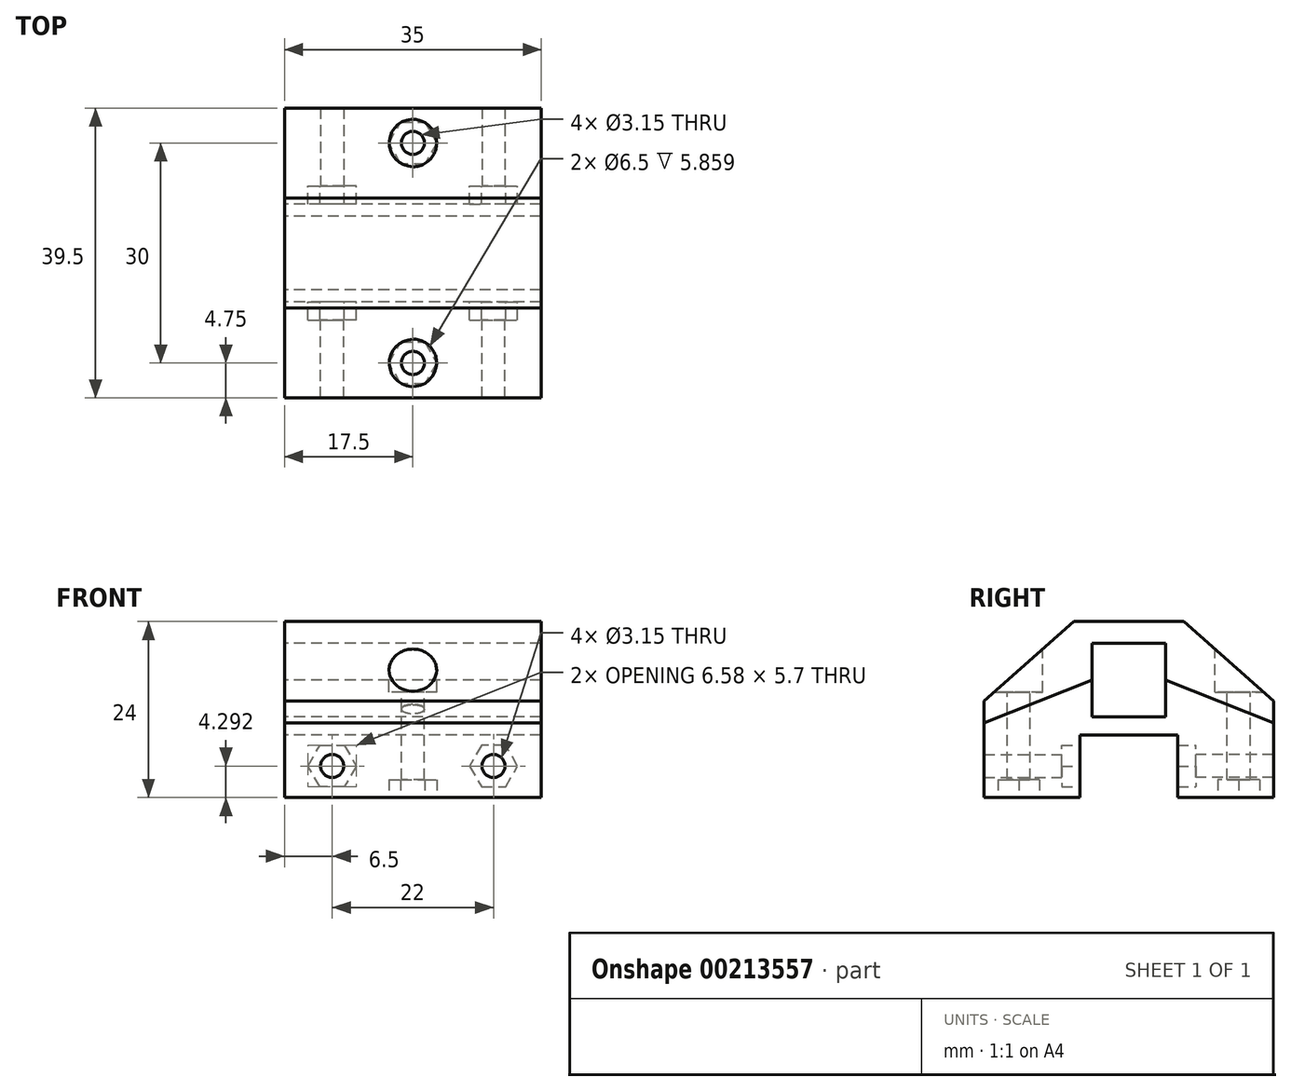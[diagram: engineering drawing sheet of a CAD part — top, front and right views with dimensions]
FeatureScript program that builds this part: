
annotation { "Feature Type Name" : "Feature", "Feature Type Description" : "" }
export const myFeature = defineFeature(function(context is Context, id is Id, definition is map)
    precondition{}
    {
        {
            var Q0;
            Q0=qCreatedBy(makeId("Right.planeOp"),FACE);
            var sketch = newSketch(context, id + "F0", { "sketchPlane" : qUnion([Q0])});
            skLineSegment(sketch, "E0", {"start": v(0, 5) * mm, "end": v(-5, 5) * mm});
            skLineSegment(sketch, "E1", {"start": v(-5, 5) * mm, "end": v(-5, 0) * mm});
            skLineSegment(sketch, "E2", {"start": v(-5, 0) * mm, "end": v(-19.75, -5.85) * mm});
            skLineSegment(sketch, "E3", {"start": v(-19.75, -5.85) * mm, "end": v(-19.75, -2.85) * mm});
            skLineSegment(sketch, "E4", {"start": v(-19.75, -2.85) * mm, "end": v(-7.5, 8) * mm});
            skLineSegment(sketch, "E5", {"start": v(-7.5, 8) * mm, "end": v(0, 8) * mm});
            skLineSegment(sketch, "E6.MirrorCS", {"start": v(5, 0) * mm, "end": v(19.75, -5.85) * mm});
            skLineSegment(sketch, "E7.MirrorCS", {"start": v(19.75, -5.85) * mm, "end": v(19.75, -2.85) * mm});
            skLineSegment(sketch, "E8.MirrorCS", {"start": v(5, 5) * mm, "end": v(5, 0) * mm});
            skLineSegment(sketch, "E9.MirrorCS", {"start": v(0, 5) * mm, "end": v(5, 5) * mm});
            skLineSegment(sketch, "E10.MirrorCS", {"start": v(7.5, 8) * mm, "end": v(0, 8) * mm});
            skLineSegment(sketch, "E11.MirrorCS", {"start": v(19.75, -2.85) * mm, "end": v(7.5, 8) * mm});
            skSolve(sketch);
        }
        {
            var Q0;
            Q0=qCreatedBy(makeId("Right.planeOp"),FACE);
            var sketch = newSketch(context, id + "F1", { "sketchPlane" : qUnion([Q0])});
            skLineSegment(sketch, "E12", {"start": v(-5, 0) * mm, "end": v(-5, -5) * mm});
            skLineSegment(sketch, "E13", {"start": v(-5, -5) * mm, "end": v(0, -5) * mm});
            skLineSegment(sketch, "E14", {"start": v(0, -5) * mm, "end": v(0, -7.5) * mm});
            skLineSegment(sketch, "E15", {"start": v(0, -7.5) * mm, "end": v(-6.66, -7.5) * mm});
            skLineSegment(sketch, "E16", {"start": v(-6.66, -7.5) * mm, "end": v(-6.66, -16) * mm});
            skLineSegment(sketch, "E17", {"start": v(-6.66, -16) * mm, "end": v(-19.75, -16) * mm});
            skLineSegment(sketch, "E18", {"start": v(-19.75, -16) * mm, "end": v(-19.75, -5.8) * mm});
            skLineSegment(sketch, "E19", {"start": v(-19.75, -5.8) * mm, "end": v(-5, 0) * mm});
            skLineSegment(sketch, "E20.MirrorCS", {"start": v(6.66, -7.5) * mm, "end": v(6.66, -16) * mm});
            skLineSegment(sketch, "E21.MirrorCS", {"start": v(6.66, -16) * mm, "end": v(19.75, -16) * mm});
            skLineSegment(sketch, "E22.MirrorCS", {"start": v(19.75, -5.8) * mm, "end": v(5, 0) * mm});
            skLineSegment(sketch, "E23.MirrorCS", {"start": v(0, -7.5) * mm, "end": v(6.66, -7.5) * mm});
            skLineSegment(sketch, "E24.MirrorCS", {"start": v(19.75, -16) * mm, "end": v(19.75, -5.8) * mm});
            skLineSegment(sketch, "E25.MirrorCS", {"start": v(5, 0) * mm, "end": v(5, -5) * mm});
            skLineSegment(sketch, "E26.MirrorCS", {"start": v(5, -5) * mm, "end": v(0, -5) * mm});
            skSolve(sketch);
        }
        {
            var Q0;
            Q0 = qSketchRegion(id + "F1", true);
            extrude(context, id + "F2", {"entities" : qUnion([Q0]), "endBound" : BoundingType.SYMMETRIC, "depth" : 35 * mm});
        }
        {
            var Q0;
            Q0=makeQuery(id+"F0.imprint","IMPRINT",FACE,{"disambiguationData":[TD([[makeQuery(id+"F0.imprint","IMPRINT",EDGE,{"derivedFrom":sQuery(id+"F0.wireOp",EDGE,"E0")}),-1.0]])]});
            extrude(context, id + "F3", {"entities" : qUnion([Q0]), "endBound" : BoundingType.SYMMETRIC, "depth" : 35 * mm});
        }
        {
            var Q0;
            Q0=qCreatedBy(makeId("Front.planeOp"),FACE);
            var sketch = newSketch(context, id + "F4", { "sketchPlane" : qUnion([Q0])});
            skLineSegment(sketch, "E27", {"start": v(0, -11.7) * mm, "end": v(-11, -11.7) * mm});
            skLineSegment(sketch, "E28", {"start": v(0, -11.7) * mm, "end": v(11, -11.7) * mm});
            skCircle(sketch, "E29.cCircle", {"center": v(-11, -11.7) * mm, "radius": 2.85 * mm, "construction": true});
            skLineSegment(sketch, "E29.0", {"start": v(-9.35, -14.56) * mm, "end": v(-12.65, -14.56) * mm});
            skLineSegment(sketch, "E29.1", {"start": v(-12.65, -14.56) * mm, "end": v(-14.3, -11.7) * mm});
            skLineSegment(sketch, "E29.2", {"start": v(-14.3, -11.7) * mm, "end": v(-12.65, -8.86) * mm});
            skLineSegment(sketch, "E29.3", {"start": v(-12.65, -8.86) * mm, "end": v(-9.35, -8.86) * mm});
            skLineSegment(sketch, "E29.4", {"start": v(-9.35, -8.86) * mm, "end": v(-7.7, -11.7) * mm});
            skLineSegment(sketch, "E29.5", {"start": v(-7.7, -11.7) * mm, "end": v(-9.35, -14.56) * mm});
            skPoint(sketch, "E29.0.midPoint", {"position": v(-11, -14.56) * mm});
            skLineSegment(sketch, "E30.MirrorCS", {"start": v(9.35, -14.56) * mm, "end": v(12.65, -14.56) * mm});
            skLineSegment(sketch, "E31.MirrorCS", {"start": v(12.65, -14.56) * mm, "end": v(14.3, -11.7) * mm});
            skPoint(sketch, "E32.MirrorP", {"position": v(11, -14.56) * mm});
            skLineSegment(sketch, "E33.MirrorCS", {"start": v(14.3, -11.7) * mm, "end": v(12.65, -8.86) * mm});
            skLineSegment(sketch, "E34.MirrorCS", {"start": v(7.7, -11.7) * mm, "end": v(9.35, -14.56) * mm});
            skLineSegment(sketch, "E35.MirrorCS", {"start": v(12.65, -8.86) * mm, "end": v(9.35, -8.86) * mm});
            skLineSegment(sketch, "E36.MirrorCS", {"start": v(9.35, -8.86) * mm, "end": v(7.7, -11.7) * mm});
            skCircle(sketch, "E37.MirrorC", {"center": v(11, -11.7) * mm, "radius": 2.85 * mm, "construction": true});
            skSolve(sketch);
        }
        {
            var Q0;
            Q0=sQuery(id+"F4.wireOp",VERTEX,"E27.end");
            var Q1;
            Q1=sQuery(id+"F4.wireOp",VERTEX,"E28.end");
            var Q2;
            Q2=makeQuery(id+"F2.opExtrude","SWEPT_BODY",BODY,{"disambiguationData":[OSD([sQuery(id+"F1.wireOp",EDGE,"E12"),sQuery(id+"F1.wireOp",EDGE,"E13"),sQuery(id+"F1.wireOp",EDGE,"E15"),sQuery(id+"F1.wireOp",EDGE,"E16"),sQuery(id+"F1.wireOp",EDGE,"E17"),sQuery(id+"F1.wireOp",EDGE,"E18"),sQuery(id+"F1.wireOp",EDGE,"E19"),sQuery(id+"F1.wireOp",EDGE,"E20.MirrorCS"),sQuery(id+"F1.wireOp",EDGE,"E21.MirrorCS"),sQuery(id+"F1.wireOp",EDGE,"E22.MirrorCS"),sQuery(id+"F1.wireOp",EDGE,"E23.MirrorCS"),sQuery(id+"F1.wireOp",EDGE,"E24.MirrorCS"),sQuery(id+"F1.wireOp",EDGE,"E25.MirrorCS"),sQuery(id+"F1.wireOp",EDGE,"E26.MirrorCS")])]});
            hole(context, id + "F5", {"style" : HoleStyle.SIMPLE, "endStyle" : HoleEndStyle.THROUGH, "oppositeDirection" : true, "standardTappedOrClearance" : lookupTablePath({ "standard" : "ISO", "fit" : "Close", "size" : "M3", "type" : "Clearance" }), "standardBlindInLast" : lookupTablePath({ "fit" : "Close", "standard" : "ISO", "size" : "M3", "type" : "Clearance" }), "holeDiameter" : 3.15 * mm, "locations" : qUnion([Q0, Q1]), "scope" : qUnion([Q2]), "isTappedThrough" : true});
        }
        {
            var Q0;
            Q0=sQuery(id+"F4.wireOp",VERTEX,"E27.end");
            var Q1;
            Q1=sQuery(id+"F4.wireOp",VERTEX,"E28.end");
            var Q2;
            Q2=makeQuery(id+"F2.opExtrude","SWEPT_BODY",BODY,{"disambiguationData":[OSD([sQuery(id+"F1.wireOp",EDGE,"E12"),sQuery(id+"F1.wireOp",EDGE,"E13"),sQuery(id+"F1.wireOp",EDGE,"E15"),sQuery(id+"F1.wireOp",EDGE,"E16"),sQuery(id+"F1.wireOp",EDGE,"E17"),sQuery(id+"F1.wireOp",EDGE,"E18"),sQuery(id+"F1.wireOp",EDGE,"E19"),sQuery(id+"F1.wireOp",EDGE,"E20.MirrorCS"),sQuery(id+"F1.wireOp",EDGE,"E21.MirrorCS"),sQuery(id+"F1.wireOp",EDGE,"E22.MirrorCS"),sQuery(id+"F1.wireOp",EDGE,"E23.MirrorCS"),sQuery(id+"F1.wireOp",EDGE,"E24.MirrorCS"),sQuery(id+"F1.wireOp",EDGE,"E25.MirrorCS"),sQuery(id+"F1.wireOp",EDGE,"E26.MirrorCS")])]});
            hole(context, id + "F6", {"style" : HoleStyle.SIMPLE, "endStyle" : HoleEndStyle.THROUGH, "standardTappedOrClearance" : lookupTablePath({ "standard" : "ISO", "fit" : "Close", "size" : "M3", "type" : "Clearance" }), "standardBlindInLast" : lookupTablePath({ "fit" : "Close", "standard" : "ISO", "size" : "M3", "type" : "Clearance" }), "holeDiameter" : 3.15 * mm, "locations" : qUnion([Q0, Q1]), "scope" : qUnion([Q2]), "isTappedThrough" : true});
        }
        {
            var Q0;
            Q0=makeQuery(id+"F4.imprint","IMPRINT",FACE,{"disambiguationData":[TD([[makeQuery(id+"F4.imprint","IMPRINT",EDGE,{"derivedFrom":sQuery(id+"F4.wireOp",EDGE,"E30.MirrorCS")}),1.0]])]});
            var Q1;
            Q1=makeQuery(id+"F4.imprint","IMPRINT",FACE,{"disambiguationData":[TD([[makeQuery(id+"F4.imprint","IMPRINT",EDGE,{"derivedFrom":sQuery(id+"F4.wireOp",EDGE,"E29.0")}),-1.0]])]});
            extrude(context, id + "F7", {"entities" : qUnion([Q0, Q1]), "endBound" : BoundingType.SYMMETRIC, "depth" : 18.32 * mm});
        }
        {
            var Q0;
            Q0=makeQuery(id+"F7.opExtrude","SWEPT_BODY",BODY,{"disambiguationData":[OSD([sQuery(id+"F4.wireOp",EDGE,"E30.MirrorCS"),sQuery(id+"F4.wireOp",EDGE,"E31.MirrorCS"),sQuery(id+"F4.wireOp",EDGE,"E33.MirrorCS"),sQuery(id+"F4.wireOp",EDGE,"E34.MirrorCS"),sQuery(id+"F4.wireOp",EDGE,"E35.MirrorCS"),sQuery(id+"F4.wireOp",EDGE,"E36.MirrorCS")])]});
            var Q1;
            Q1=makeQuery(id+"F2.opExtrude","SWEPT_BODY",BODY,{"disambiguationData":[OSD([sQuery(id+"F1.wireOp",EDGE,"E12"),sQuery(id+"F1.wireOp",EDGE,"E13"),sQuery(id+"F1.wireOp",EDGE,"E15"),sQuery(id+"F1.wireOp",EDGE,"E16"),sQuery(id+"F1.wireOp",EDGE,"E17"),sQuery(id+"F1.wireOp",EDGE,"E18"),sQuery(id+"F1.wireOp",EDGE,"E19"),sQuery(id+"F1.wireOp",EDGE,"E20.MirrorCS"),sQuery(id+"F1.wireOp",EDGE,"E21.MirrorCS"),sQuery(id+"F1.wireOp",EDGE,"E22.MirrorCS"),sQuery(id+"F1.wireOp",EDGE,"E23.MirrorCS"),sQuery(id+"F1.wireOp",EDGE,"E24.MirrorCS"),sQuery(id+"F1.wireOp",EDGE,"E25.MirrorCS"),sQuery(id+"F1.wireOp",EDGE,"E26.MirrorCS")])]});
            booleanBodies(context, id + "F8", {"operationType" : BooleanOperationType.SUBTRACTION, "tools" : qUnion([Q0]), "targets" : qUnion([Q1])});
        }
        {
            var Q0;
            Q0=makeQuery(id+"F7.opExtrude","SWEPT_BODY",BODY,{"disambiguationData":[OSD([sQuery(id+"F4.wireOp",EDGE,"E29.0"),sQuery(id+"F4.wireOp",EDGE,"E29.1"),sQuery(id+"F4.wireOp",EDGE,"E29.2"),sQuery(id+"F4.wireOp",EDGE,"E29.3"),sQuery(id+"F4.wireOp",EDGE,"E29.4"),sQuery(id+"F4.wireOp",EDGE,"E29.5")])]});
            var Q1;
            Q1=makeQuery(id+"F2.opExtrude","SWEPT_BODY",BODY,{"disambiguationData":[OSD([sQuery(id+"F1.wireOp",EDGE,"E12"),sQuery(id+"F1.wireOp",EDGE,"E13"),sQuery(id+"F1.wireOp",EDGE,"E15"),sQuery(id+"F1.wireOp",EDGE,"E16"),sQuery(id+"F1.wireOp",EDGE,"E17"),sQuery(id+"F1.wireOp",EDGE,"E18"),sQuery(id+"F1.wireOp",EDGE,"E19"),sQuery(id+"F1.wireOp",EDGE,"E20.MirrorCS"),sQuery(id+"F1.wireOp",EDGE,"E21.MirrorCS"),sQuery(id+"F1.wireOp",EDGE,"E22.MirrorCS"),sQuery(id+"F1.wireOp",EDGE,"E23.MirrorCS"),sQuery(id+"F1.wireOp",EDGE,"E24.MirrorCS"),sQuery(id+"F1.wireOp",EDGE,"E25.MirrorCS"),sQuery(id+"F1.wireOp",EDGE,"E26.MirrorCS")])]});
            booleanBodies(context, id + "F9", {"operationType" : BooleanOperationType.SUBTRACTION, "tools" : qUnion([Q0]), "targets" : qUnion([Q1])});
        }
        {
            var Q0;
            Q0=qCreatedBy(makeId("Top.planeOp"),FACE);
            var Q1;
            Q1 = qBodyType(qCreatedBy(id + "F11" ,EDGE), BodyType.WIRE);
            cPlane(context, id + "F10", {"entities" : qUnion([Q0, Q1]), "cplaneType" : CPlaneType.OFFSET, "offset" : 15 * mm, "width" : 150 * mm, "height" : 150 * mm});
        }
        {
            var Q0;
            Q0=qCreatedBy(id+"F10.planeOp",FACE);
            var sketch = newSketch(context, id + "F11", { "sketchPlane" : qUnion([Q0])});
            skLineSegment(sketch, "E38", {"start": v(0, 0) * mm, "end": v(0, 15) * mm, "construction": true});
            skLineSegment(sketch, "E39", {"start": v(0, 0) * mm, "end": v(0, -15) * mm, "construction": true});
            skSolve(sketch);
        }
        {
            var Q0;
            Q0=sQuery(id+"F11.wireOp",VERTEX,"E38.end");
            var Q1;
            Q1=sQuery(id+"F11.wireOp",VERTEX,"E39.end");
            var Q2;
            Q2=makeQuery(id+"F2.opExtrude","SWEPT_BODY",BODY,{"disambiguationData":[OSD([sQuery(id+"F1.wireOp",EDGE,"E12"),sQuery(id+"F1.wireOp",EDGE,"E13"),sQuery(id+"F1.wireOp",EDGE,"E15"),sQuery(id+"F1.wireOp",EDGE,"E16"),sQuery(id+"F1.wireOp",EDGE,"E17"),sQuery(id+"F1.wireOp",EDGE,"E18"),sQuery(id+"F1.wireOp",EDGE,"E19"),sQuery(id+"F1.wireOp",EDGE,"E20.MirrorCS"),sQuery(id+"F1.wireOp",EDGE,"E21.MirrorCS"),sQuery(id+"F1.wireOp",EDGE,"E22.MirrorCS"),sQuery(id+"F1.wireOp",EDGE,"E23.MirrorCS"),sQuery(id+"F1.wireOp",EDGE,"E24.MirrorCS"),sQuery(id+"F1.wireOp",EDGE,"E25.MirrorCS"),sQuery(id+"F1.wireOp",EDGE,"E26.MirrorCS")])]});
            var Q3;
            Q3=makeQuery(id+"F3.opExtrude","SWEPT_BODY",BODY,{"disambiguationData":[OSD([sQuery(id+"F0.wireOp",EDGE,"E0"),sQuery(id+"F0.wireOp",EDGE,"E1"),sQuery(id+"F0.wireOp",EDGE,"E2"),sQuery(id+"F0.wireOp",EDGE,"E3"),sQuery(id+"F0.wireOp",EDGE,"E4"),sQuery(id+"F0.wireOp",EDGE,"E5"),sQuery(id+"F0.wireOp",EDGE,"E6.MirrorCS"),sQuery(id+"F0.wireOp",EDGE,"E7.MirrorCS"),sQuery(id+"F0.wireOp",EDGE,"E8.MirrorCS"),sQuery(id+"F0.wireOp",EDGE,"E9.MirrorCS"),sQuery(id+"F0.wireOp",EDGE,"E10.MirrorCS"),sQuery(id+"F0.wireOp",EDGE,"E11.MirrorCS")])]});
            hole(context, id + "F12", {"style" : HoleStyle.C_BORE, "endStyle" : HoleEndStyle.THROUGH, "holeDiameter" : 3.15 * mm, "cBoreDiameter" : 6.5 * mm, "cBoreDepth" : .1 * mm, "locations" : qUnion([Q0, Q1]), "scope" : qUnion([Q2, Q3]), "isTappedThrough" : true});
        }
        {
            var Q0;
            Q0=qCreatedBy(makeId("Top.planeOp"),FACE);
            cPlane(context, id + "F13", {"entities" : qUnion([Q0]), "cplaneType" : CPlaneType.OFFSET, "offset" : 17.05 * mm, "oppositeDirection" : true, "width" : 150 * mm, "height" : 150 * mm});
        }
        {
            var Q0;
            Q0=qCreatedBy(id+"F13.planeOp",FACE);
            var sketch = newSketch(context, id + "F14", { "sketchPlane" : qUnion([Q0])});
            skLineSegment(sketch, "E40", {"start": v(0, 0) * mm, "end": v(0, -15) * mm, "construction": true});
            skCircle(sketch, "E41.cCircle", {"center": v(0, -15) * mm, "radius": 2.85 * mm, "construction": true});
            skLineSegment(sketch, "E41.0", {"start": v(1.65, -12.15) * mm, "end": v(3.3, -15) * mm});
            skLineSegment(sketch, "E41.1", {"start": v(3.3, -15) * mm, "end": v(1.65, -17.85) * mm});
            skLineSegment(sketch, "E41.2", {"start": v(1.65, -17.85) * mm, "end": v(-1.65, -17.85) * mm});
            skLineSegment(sketch, "E41.3", {"start": v(-1.65, -17.85) * mm, "end": v(-3.3, -15) * mm});
            skLineSegment(sketch, "E41.4", {"start": v(-3.3, -15) * mm, "end": v(-1.65, -12.15) * mm});
            skLineSegment(sketch, "E41.5", {"start": v(-1.65, -12.15) * mm, "end": v(1.65, -12.15) * mm});
            skPoint(sketch, "E41.0.midPoint", {"position": v(2.47, -13.57) * mm});
            skLineSegment(sketch, "E42", {"start": v(0, 0) * mm, "end": v(-18.25, 0) * mm, "construction": true});
            skLineSegment(sketch, "E43.MirrorCS", {"start": v(1.65, 17.85) * mm, "end": v(-1.65, 17.85) * mm});
            skLineSegment(sketch, "E44.MirrorCS", {"start": v(3.3, 15) * mm, "end": v(1.65, 17.85) * mm});
            skLineSegment(sketch, "E45.MirrorCS", {"start": v(0, 0) * mm, "end": v(0, 15) * mm, "construction": true});
            skPoint(sketch, "E46.MirrorP", {"position": v(2.47, 13.58) * mm});
            skLineSegment(sketch, "E47.MirrorCS", {"start": v(-3.3, 15) * mm, "end": v(-1.65, 12.15) * mm});
            skLineSegment(sketch, "E48.MirrorCS", {"start": v(-1.65, 12.15) * mm, "end": v(1.65, 12.15) * mm});
            skCircle(sketch, "E49.MirrorC", {"center": v(0, 15) * mm, "radius": 2.85 * mm, "construction": true});
            skLineSegment(sketch, "E50.MirrorCS", {"start": v(-1.65, 17.85) * mm, "end": v(-3.3, 15) * mm});
            skLineSegment(sketch, "E51.MirrorCS", {"start": v(1.65, 12.15) * mm, "end": v(3.3, 15) * mm});
            skSolve(sketch);
        }
        {
            var Q0;
            Q0 = qSketchRegion(id + "F14", true);
            extrude(context, id + "F15", {"entities" : qUnion([Q0]), "depth" : 3.5 * mm});
        }
        {
            var Q0;
            Q0=makeQuery(id+"F15.opExtrude","SWEPT_BODY",BODY,{"disambiguationData":[OSD([sQuery(id+"F14.wireOp",EDGE,"E41.0"),sQuery(id+"F14.wireOp",EDGE,"E41.1"),sQuery(id+"F14.wireOp",EDGE,"E41.2"),sQuery(id+"F14.wireOp",EDGE,"E41.3"),sQuery(id+"F14.wireOp",EDGE,"E41.4"),sQuery(id+"F14.wireOp",EDGE,"E41.5")])]});
            var Q1;
            Q1=makeQuery(id+"F2.opExtrude","SWEPT_BODY",BODY,{"disambiguationData":[OSD([sQuery(id+"F1.wireOp",EDGE,"E12"),sQuery(id+"F1.wireOp",EDGE,"E13"),sQuery(id+"F1.wireOp",EDGE,"E15"),sQuery(id+"F1.wireOp",EDGE,"E16"),sQuery(id+"F1.wireOp",EDGE,"E17"),sQuery(id+"F1.wireOp",EDGE,"E18"),sQuery(id+"F1.wireOp",EDGE,"E19"),sQuery(id+"F1.wireOp",EDGE,"E20.MirrorCS"),sQuery(id+"F1.wireOp",EDGE,"E21.MirrorCS"),sQuery(id+"F1.wireOp",EDGE,"E22.MirrorCS"),sQuery(id+"F1.wireOp",EDGE,"E23.MirrorCS"),sQuery(id+"F1.wireOp",EDGE,"E24.MirrorCS"),sQuery(id+"F1.wireOp",EDGE,"E25.MirrorCS"),sQuery(id+"F1.wireOp",EDGE,"E26.MirrorCS")])]});
            booleanBodies(context, id + "F16", {"operationType" : BooleanOperationType.SUBTRACTION, "tools" : qUnion([Q0]), "targets" : qUnion([Q1])});
        }
        {
            var Q0;
            Q0=makeQuery(id+"F15.opExtrude","SWEPT_BODY",BODY,{"disambiguationData":[OSD([sQuery(id+"F14.wireOp",EDGE,"E43.MirrorCS"),sQuery(id+"F14.wireOp",EDGE,"E44.MirrorCS"),sQuery(id+"F14.wireOp",EDGE,"E47.MirrorCS"),sQuery(id+"F14.wireOp",EDGE,"E48.MirrorCS"),sQuery(id+"F14.wireOp",EDGE,"E50.MirrorCS"),sQuery(id+"F14.wireOp",EDGE,"E51.MirrorCS")])]});
            var Q1;
            Q1=makeQuery(id+"F2.opExtrude","SWEPT_BODY",BODY,{"disambiguationData":[OSD([sQuery(id+"F1.wireOp",EDGE,"E12"),sQuery(id+"F1.wireOp",EDGE,"E13"),sQuery(id+"F1.wireOp",EDGE,"E15"),sQuery(id+"F1.wireOp",EDGE,"E16"),sQuery(id+"F1.wireOp",EDGE,"E17"),sQuery(id+"F1.wireOp",EDGE,"E18"),sQuery(id+"F1.wireOp",EDGE,"E19"),sQuery(id+"F1.wireOp",EDGE,"E20.MirrorCS"),sQuery(id+"F1.wireOp",EDGE,"E21.MirrorCS"),sQuery(id+"F1.wireOp",EDGE,"E22.MirrorCS"),sQuery(id+"F1.wireOp",EDGE,"E23.MirrorCS"),sQuery(id+"F1.wireOp",EDGE,"E24.MirrorCS"),sQuery(id+"F1.wireOp",EDGE,"E25.MirrorCS"),sQuery(id+"F1.wireOp",EDGE,"E26.MirrorCS")])]});
            booleanBodies(context, id + "F17", {"operationType" : BooleanOperationType.SUBTRACTION, "tools" : qUnion([Q0]), "targets" : qUnion([Q1])});
        }
    });
